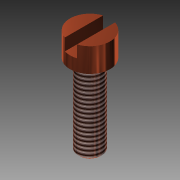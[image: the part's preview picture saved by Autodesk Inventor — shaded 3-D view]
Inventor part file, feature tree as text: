
AUTODESK INVENTOR PART (.ipt)
format: ipt  version: 2015 (Build 190159000, 159)  size: 102,912 bytes
history: native  units: mm
features: extrude x3, sketch x3, thread x1, chamfer x1
ambient origin geometry x8: Origin, YZ Plane, XZ Plane, XY Plane, X Axis, Y Axis, Z Axis, Center Point
bodies: 实体1 (feature_tree)
feature tree (8):
  extrude  "拉伸1"  Depth=3.0mm TaperAngle=0.0deg
  extrude  "拉伸2"  Depth=1.5mm TaperAngle=0.0deg
  extrude  "拉伸3"  Depth=10.0mm TaperAngle=0.0deg
  thread  "螺纹1"  [1 undecoded]
  chamfer  "倒角1"  Distance=0.2mm Angle=45.0deg
  sketch  "草图1"  dims[d0=5.0mm d1=3.0mm d2=0.0mm]
  sketch  "草图2"  dims[d3=1.5mm d4=1.5mm d5=0.0mm]
  sketch  "草图3"  dims[d6=3.0mm d7=10.0mm d8=0.0mm d9=10.0mm d10=0.0mm d11=0.2mm d12=2.0mm d13=45.0deg]
note: 1 required parameter value undecoded (feature->parameter linkage not recoverable at this tier; creation-order binding heuristic only, values carry confidence <= 0.55)
